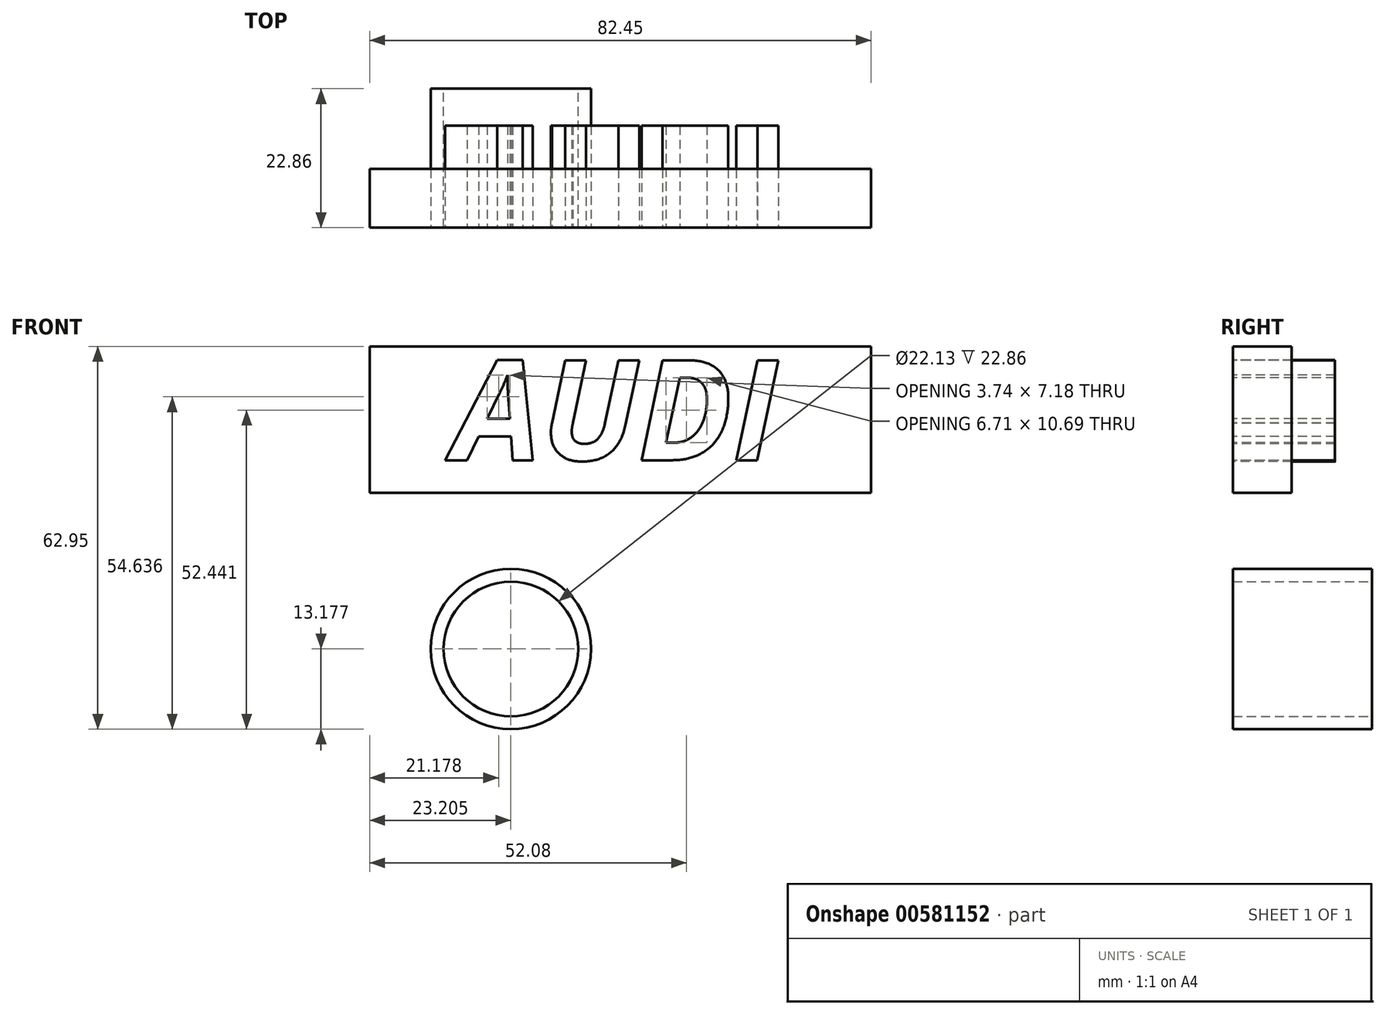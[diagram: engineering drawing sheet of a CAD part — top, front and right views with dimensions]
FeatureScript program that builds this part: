
annotation { "Feature Type Name" : "Feature", "Feature Type Description" : "" }
export const myFeature = defineFeature(function(context is Context, id is Id, definition is map)
    precondition{}
    {
        {
            var Q0;
            Q0=qCreatedBy(makeId("Front.planeOp"),FACE);
            var sketch = newSketch(context, id + "F0", { "sketchPlane" : qUnion([Q0])});
            skText(sketch, "E0", { "text": "AUDI", "fontName": "OpenSans-BoldItalic.ttf"});
            const initialGuessF0  = {"E0": [-0.04777, 0.02234, 1, 0, 0.01656]};
            skSetInitialGuess(sketch, initialGuessF0);
            skSolve(sketch);
        }
        {
            var Q0;
            Q0 = qSketchRegion(id + "F0", true);
            extrude(context, id + "F1", {"entities" : qUnion([Q0]), "oppositeDirection" : true, "depth" : 16.76 * mm, "offsetDistance" : 25.4 * mm});
        }
        {
            var Q0;
            Q0=qCreatedBy(makeId("Front.planeOp"),FACE);
            var sketch = newSketch(context, id + "F2", { "sketchPlane" : qUnion([Q0])});
            skLineSegment(sketch, "E1.bottom", {"start": v(-61.53, 41.07) * mm, "end": v(20.92, 41.07) * mm});
            skLineSegment(sketch, "E1.top", {"start": v(-61.53, 16.95) * mm, "end": v(20.92, 16.95) * mm});
            skLineSegment(sketch, "E1.left", {"start": v(-61.53, 41.07) * mm, "end": v(-61.53, 16.95) * mm});
            skLineSegment(sketch, "E1.right", {"start": v(20.92, 41.07) * mm, "end": v(20.92, 16.95) * mm});
            skSolve(sketch);
        }
        {
            var Q0;
            Q0 = qSketchRegion(id + "F2", true);
            extrude(context, id + "F3", {"entities" : qUnion([Q0]), "oppositeDirection" : true, "depth" : 9.65 * mm, "offsetDistance" : 25.4 * mm});
        }
        {
            var Q0;
            Q0=qCreatedBy(makeId("Front.planeOp"),FACE);
            var sketch = newSketch(context, id + "F4", { "sketchPlane" : qUnion([Q0])});
            skCircle(sketch, "E2", {"center": v(-38.33, -8.7) * mm, "radius": 13.17 * mm});
            skSolve(sketch);
        }
        {
            var Q0;
            Q0 = qSketchRegion(id + "F4", true);
            extrude(context, id + "F5", {"entities" : qUnion([Q0]), "oppositeDirection" : true, "depth" : 22.86 * mm, "offsetDistance" : 25.4 * mm});
        }
        {
            var Q0;
            Q0=makeQuery(id+"F5.opExtrude","CAP_FACE",FACE,{"disambiguationData":[OSD([sQuery(id+"F4.wireOp",EDGE,"E2")])],"isStart":true});
            var sketch = newSketch(context, id + "F6", { "sketchPlane" : qUnion([Q0])});
            skCircle(sketch, "E3", {"center": v(-38.33, -8.7) * mm, "radius": 11.34 * mm});
            skSolve(sketch);
        }
        {
            var Q0;
            Q0 = qSketchRegion(id + "F6", true);
            extrude(context, id + "F7", {"entities" : qUnion([Q0]), "operationType" : NewBodyOperationType.REMOVE, "depth" : 64.52 * mm, "offsetDistance" : 25.4 * mm});
        }
        {
            var Q0;
            Q0=makeQuery(id+"F5.opExtrude","CAP_FACE",FACE,{"disambiguationData":[OSD([sQuery(id+"F4.wireOp",EDGE,"E2")])],"isStart":true});
            var sketch = newSketch(context, id + "F8", { "sketchPlane" : qUnion([Q0])});
            skCircle(sketch, "E4", {"center": v(-38.33, -8.7) * mm, "radius": 12.02 * mm});
            skSolve(sketch);
        }
        {
            var Q0;
            Q0 = qSketchRegion(id + "F8", true);
            extrude(context, id + "F9", {"entities" : qUnion([Q0]), "operationType" : NewBodyOperationType.REMOVE, "depth" : 40.9 * mm, "offsetDistance" : 25.4 * mm});
        }
        {
            var Q0;
            Q0=makeQuery(id+"F5.opExtrude","CAP_FACE",FACE,{"disambiguationData":[OSD([sQuery(id+"F4.wireOp",EDGE,"E2")])],"isStart":true});
            var sketch = newSketch(context, id + "F10", { "sketchPlane" : qUnion([Q0])});
            skCircle(sketch, "E5", {"center": v(-38.33, -8.7) * mm, "radius": 10.67 * mm});
            skSolve(sketch);
        }
        {
            var Q0;
            Q0 = qSketchRegion(id + "F10", true);
            extrude(context, id + "F11", {"entities" : qUnion([Q0]), "operationType" : NewBodyOperationType.REMOVE, "depth" : 33.02 * mm, "offsetDistance" : 25.4 * mm});
        }
        {
            var Q0;
            Q0=makeQuery(id+"F5.opExtrude","CAP_FACE",FACE,{"disambiguationData":[OSD([sQuery(id+"F4.wireOp",EDGE,"E2")])],"isStart":false});
            var sketch = newSketch(context, id + "F12", { "sketchPlane" : qUnion([Q0])});
            skCircle(sketch, "E6", {"center": v(38.33, -8.7) * mm, "radius": 11.07 * mm});
            skSolve(sketch);
        }
        {
            var Q0;
            Q0 = qSketchRegion(id + "F12", true);
            extrude(context, id + "F13", {"entities" : qUnion([Q0]), "operationType" : NewBodyOperationType.REMOVE, "oppositeDirection" : true, "depth" : 84.58 * mm, "offsetDistance" : 25.4 * mm});
        }
    });
